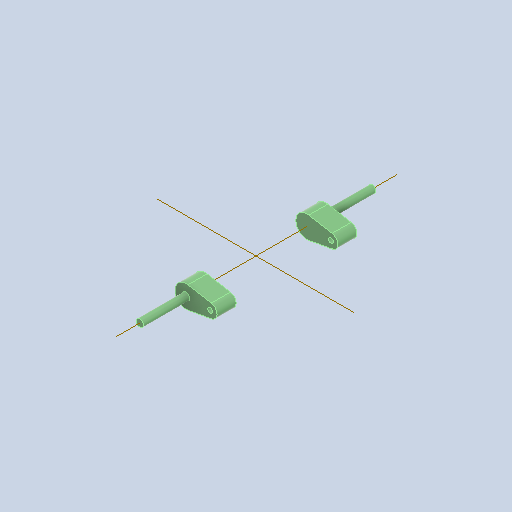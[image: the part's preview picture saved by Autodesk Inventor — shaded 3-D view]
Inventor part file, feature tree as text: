
AUTODESK INVENTOR PART (.ipt)
format: ipt  version: 2025 (Build 290162000, 162)  size: 144,896 bytes
history: native  units: mm
features: sketch x5, extrude x3, other x2, hole x2, plane x1, mirror x1
ambient origin geometry x8: Origin, YZ Plane, XZ Plane, XY Plane, X Axis, Y Axis, Z Axis, Center Point
bodies: Body1 (feature_tree)
feature tree (14):
  parser-record x1  (decoder bookkeeping rows leaked as tree rows — omitted from the tree; the rows remain in map.json)
  other  "實體1"
  plane  "工作平面2"
  extrude  "擠出1"  Depth=130.0mm
  extrude  "擠出2"  Depth=60.0mm
  extrude  "擠出3"  Depth=37.5mm
  hole  "孔1"  [1 undecoded]
  hole  "孔2"  [1 undecoded]
  mirror  "鏡射2"
  sketch  "草圖1"
  sketch  "草圖2"
  sketch  "草圖3"
  sketch  "草圖4"
  sketch  "草圖5"
note: 2 required parameter values undecoded (feature->parameter linkage not recoverable at this tier; creation-order binding heuristic only, values carry confidence <= 0.55)
note: 1 file-system path scrubbed to <path> (originals preserved in map.json)
